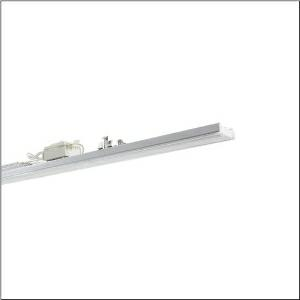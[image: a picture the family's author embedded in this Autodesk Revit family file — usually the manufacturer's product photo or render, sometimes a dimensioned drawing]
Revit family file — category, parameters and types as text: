
# Revit family: licross_r__21_recessed_ho_51te12vn4cxm_165e
name_source: partatom
category: Lighting Fixtures
units: mm (PartAtom-declared; Revit-internal decimal feet)

## family parameters
Cut with Voids When Loaded = No
Host = Face
Light Source = No
Part Type = Normal
Room Calculation Point = No
Round Connector Dimension = Use Diameter
Shared = No

## types (1)
- --- (1 x LED, 12000 lm, 64.8 W, 4000K)
    Apparent Load = 65 VA
    CIE Flux Codes = 66 91 98 100 100
    Color Rendering = 80
    Color Temperature = 4000K
    Default Elevation = 1800 mm
    Description = Licross® 21 Recessed HO, luminaire insert, of sheet steel, galvanised, coil coated, white, length: 1.500mm, width: 66mm, height: 67mm, LED rated luminous flux: 12.000lm, light colour: 840, control gear: DALI 2, CLO, with plug, 5-pole, with phase selection, mains connection: 220..240V, AC, 50/60Hz, start of lifetime: 65W, end of service life: 72W, internal wiring halogen-free, primary optical cover: cover, of PMMA, light emission: direct distribution, primary light characteristic: symmetric, protection rating (complete): IP54, insulation class (complete): insulation class I (protective earthing), certification: CE, ENEC, VDE, UKCA, protection symbol: D if used in an environment with non-conductive dust loads with corresponding accessories, impact resistance: IK06, permissible ambient temperature for indoor applications: -25..+30°C, corresponds to IFS (International Featured Standards) requirements for safety and quality in the food industry, reducing of maximum allowable ambient temperature of 5°C with ceiling mounting, LABS conformity tested according to VDMA 24364:2018-05, packaging unit: 1 piece
    Height = 58 mm
    Lamp = 1 x LED
    Lamp Light Flux = 12000 lm
    Lamp Power = 64.8 W
    Lamp count = 1
    Length = 1500 mm
    Luminous efficacy = 185 lm/W
    Manufacturer = Siteco
    ModVariant = No
    Model = 51TE12VN4CXM
    Mounting Place = Ceiling
    Mounting Type = Pendant
    Number of Poles = 1
    OnlyDefault = Yes
    Power Factor = 1
    Product Name = Licross® 21 Recessed HO
    Product group = luminaire insert | ceiling pendant
    ProductGroupID = 902
    Protection Class = Protection class I
    Protection Degree = IP 54
    RLX_Detail_Level = 1
    RLX_Emergency_Light_Flux = 0 lm
    RLX_Emergency_Type = 0
    RLX_Emergency_Type_DB = No
    RlxData = <blob elided: 24629 chars, md5=903d9929>
    Socket = socket
    Standby Power = 0 W
    System Light Flux = 12000 lm
    System Power = 65 W
    Type Comments = factory setting: luminous flux: 100 % | dim-lin: 254 | 441 mA
    Type Image = l_1296930.jpg
    URL = http://relux.com
    VarID = @adj_108691
    Voltage = 0 V
    Weight = 0.00 kg
    Width = 66 mm

## geometry (parser evidence)
native form markers: Blend x4, Sweep x12
no freeform markers — native parametric forms only
